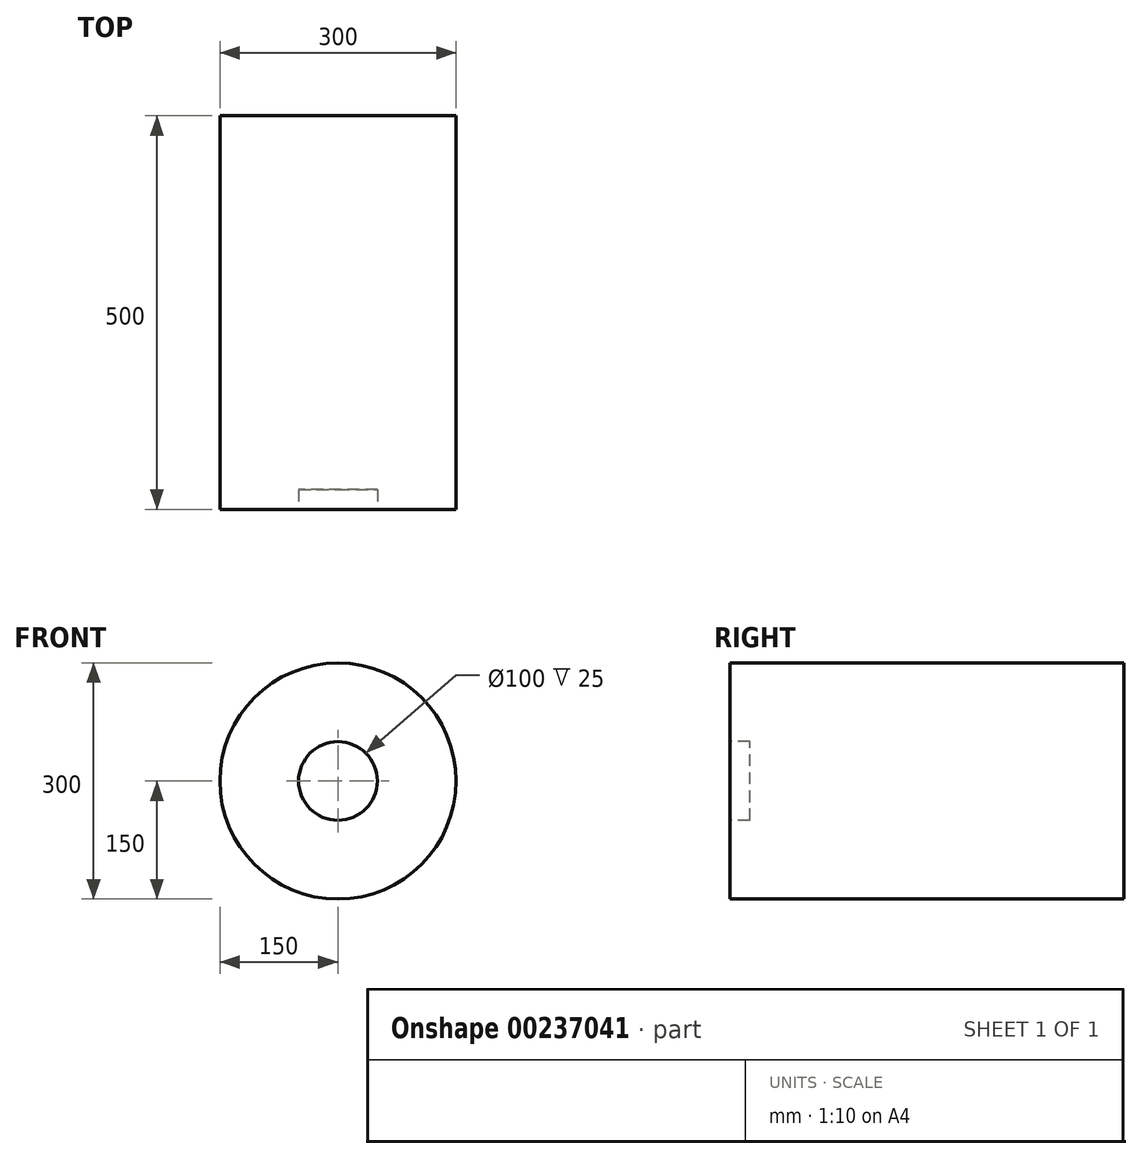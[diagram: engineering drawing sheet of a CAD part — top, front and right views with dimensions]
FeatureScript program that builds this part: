
annotation { "Feature Type Name" : "Feature", "Feature Type Description" : "" }
export const myFeature = defineFeature(function(context is Context, id is Id, definition is map)
    precondition{}
    {
        {
            var Q0;
            Q0=qCreatedBy(makeId("Front.planeOp"),FACE);
            var sketch = newSketch(context, id + "F0", { "sketchPlane" : qUnion([Q0])});
            skCircle(sketch, "E0", {"center": v(0, 0) * mm, "radius": 150 * mm});
            skSolve(sketch);
        }
        {
            var Q0;
            Q0=qCreatedBy(makeId("Front.planeOp"),FACE);
            var sketch = newSketch(context, id + "F1", { "sketchPlane" : qUnion([Q0])});
            skCircle(sketch, "E1", {"center": v(0, 0) * mm, "radius": 50 * mm});
            skSolve(sketch);
        }
        {
            var Q0;
            Q0=qSketchRegion(id+"F0",true);
            extrude(context, id + "F2", {"entities" : qUnion([Q0]), "oppositeDirection" : true, "depth" : 500 * mm});
        }
        {
            var Q0;
            Q0 = qSketchRegion(id + "F1", true);
            extrude(context, id + "F3", {"entities" : qUnion([Q0]), "operationType" : NewBodyOperationType.REMOVE, "oppositeDirection" : true, "depth" : 25 * mm});
        }
    });
